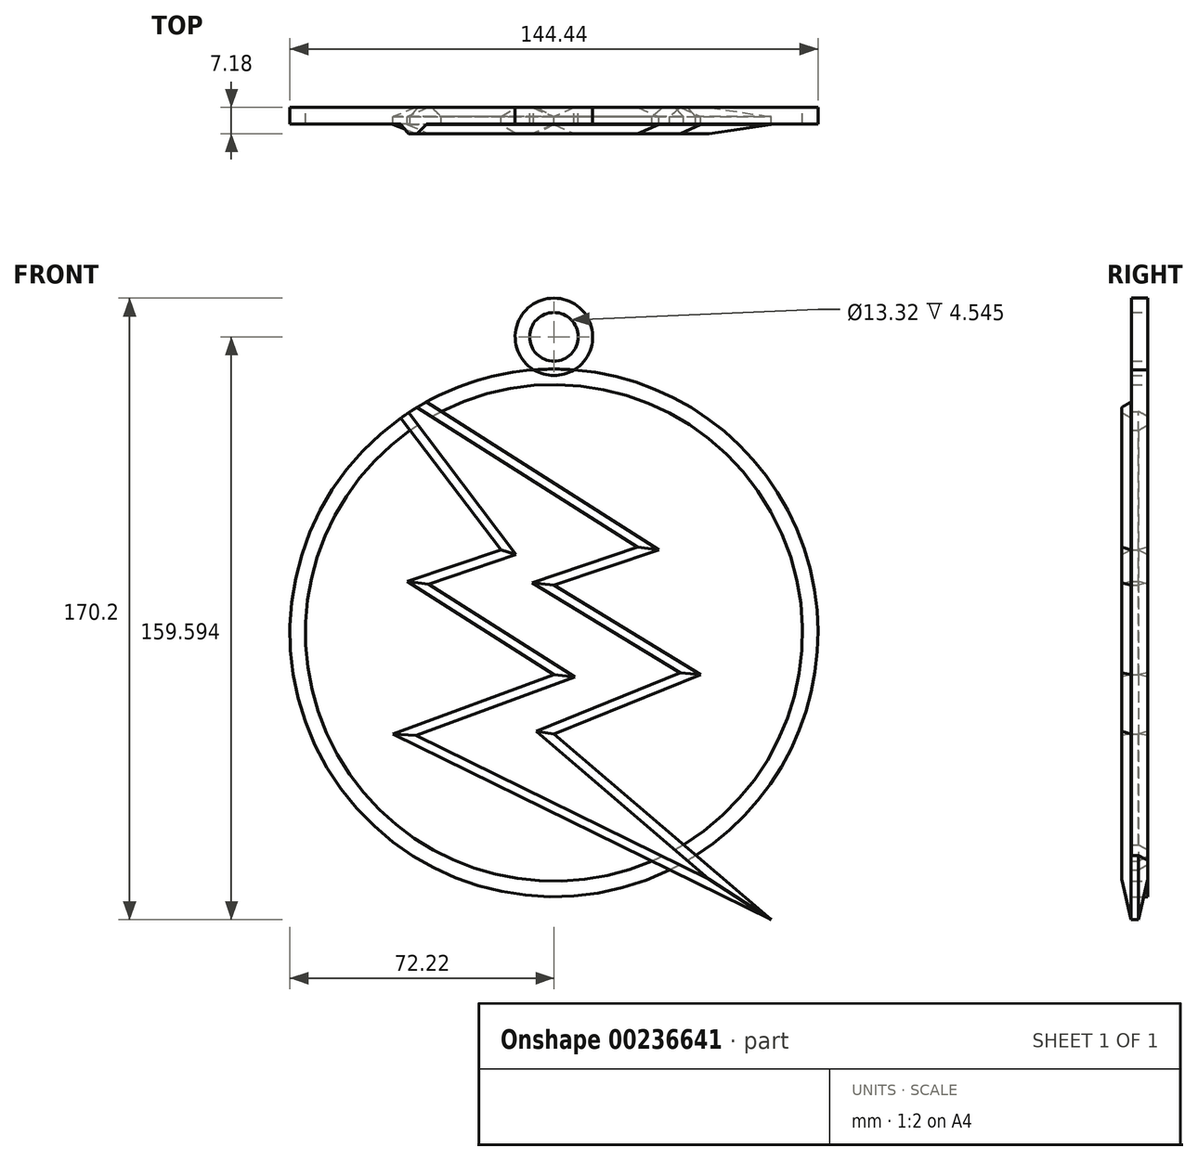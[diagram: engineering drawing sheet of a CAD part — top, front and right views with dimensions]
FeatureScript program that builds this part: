
annotation { "Feature Type Name" : "Feature", "Feature Type Description" : "" }
export const myFeature = defineFeature(function(context is Context, id is Id, definition is map)
    precondition{}
    {
        {
            var Q0;
            Q0=qCreatedBy(makeId("Front.planeOp"),FACE);
            var sketch = newSketch(context, id + "F0", { "sketchPlane" : qUnion([Q0])});
            skCircle(sketch, "E0", {"center": v(0, 0) * mm, "radius": 72.22 * mm});
            skCircle(sketch, "E1", {"center": v(0, 0) * mm, "radius": 67.99 * mm});
            skLineSegment(sketch, "E2", {"start": v(-54.7, 75.8) * mm, "end": v(28.75, 22.73) * mm});
            skLineSegment(sketch, "E3", {"start": v(28.75, 22.73) * mm, "end": v(0, 13.04) * mm});
            skLineSegment(sketch, "E4", {"start": v(0, 13.04) * mm, "end": v(40.2, -11.4) * mm});
            skLineSegment(sketch, "E5", {"start": v(40.2, -11.4) * mm, "end": v(0, -27.72) * mm});
            skLineSegment(sketch, "E6", {"start": v(0, -27.72) * mm, "end": v(59.4, -78.53) * mm});
            skLineSegment(sketch, "E7", {"start": v(59.4, -78.53) * mm, "end": v(-44.1, -27.72) * mm});
            skLineSegment(sketch, "E8", {"start": v(-44.1, -27.72) * mm, "end": v(0, -11.4) * mm});
            skLineSegment(sketch, "E9", {"start": v(0, -11.4) * mm, "end": v(-40.11, 14.1) * mm});
            skLineSegment(sketch, "E10", {"start": v(-40.11, 14.1) * mm, "end": v(-14.52, 22.73) * mm});
            skLineSegment(sketch, "E11", {"start": v(-14.52, 22.73) * mm, "end": v(-54.7, 75.8) * mm});
            skCircle(sketch, "E12", {"center": v(0, 81.06) * mm, "radius": 10.6 * mm});
            skCircle(sketch, "E13", {"center": v(0, 81.06) * mm, "radius": 6.66 * mm});
            skSolve(sketch);
        }
        {
            var Q0;
            {var subQ0=sQuery(id+"F0.wireOp",EDGE,"E11");var subQ1=sQuery(id+"F0.wireOp",EDGE,"E0");var subQ2=makeQuery(id+"F0.imprint","INTERSECT",VERTEX,{"derivedFrom":[subQ1,subQ0]});Q0=makeQuery(id+"F0.imprint","IMPRINT",FACE,{"disambiguationData":[TD([[makeQuery(id+"F0.imprint","IMPRINT",EDGE,{"disambiguationData":[TD([[subQ2,1.0]])],"derivedFrom":subQ1}),-1.0]])]});}
            var sketch = newSketch(context, id + "F1", { "sketchPlane" : qUnion([Q0])});
            skSolve(sketch);
        }
        {
            var Q0;
            {var subQ11=sQuery(id+"F0.wireOp",EDGE,"E3");Q0=makeQuery(id+"F0.imprint","IMPRINT",FACE,{"disambiguationData":[TD([[makeQuery(id+"F0.imprint","IMPRINT",EDGE,{"derivedFrom":subQ11}),-1.0]])]});}
            var Q1;
            {var subQ0=sQuery(id+"F0.wireOp",EDGE,"E7");var subQ1=sQuery(id+"F0.wireOp",EDGE,"E0");var subQ2=makeQuery(id+"F0.imprint","INTERSECT",VERTEX,{"derivedFrom":[subQ1,subQ0]});Q1=makeQuery(id+"F0.imprint","IMPRINT",FACE,{"disambiguationData":[TD([[makeQuery(id+"F0.imprint","IMPRINT",EDGE,{"disambiguationData":[TD([[subQ2,-1.0]])],"derivedFrom":subQ1}),1.0]])]});}
            var Q2;
            {var subQ0=sQuery(id+"F0.wireOp",EDGE,"E7");var subQ1=sQuery(id+"F0.wireOp",EDGE,"E0");var subQ2=makeQuery(id+"F0.imprint","INTERSECT",VERTEX,{"derivedFrom":[subQ1,subQ0]});Q2=makeQuery(id+"F0.imprint","IMPRINT",FACE,{"disambiguationData":[TD([[makeQuery(id+"F0.imprint","IMPRINT",EDGE,{"disambiguationData":[TD([[subQ2,-1.0]])],"derivedFrom":subQ1}),-1.0]])]});}
            var Q3;
            {var subQ0=sQuery(id+"F0.wireOp",EDGE,"E11");var subQ1=sQuery(id+"F0.wireOp",EDGE,"E0");var subQ2=makeQuery(id+"F0.imprint","INTERSECT",VERTEX,{"derivedFrom":[subQ1,subQ0]});Q3=makeQuery(id+"F1.imprint","IMPRINT",FACE,{"disambiguationData":[TD([[makeQuery(id+"F1.imprint","IMPRINT",EDGE,{"derivedFrom":makeQuery(id+"F0.imprint","IMPRINT",EDGE,{"disambiguationData":[TD([[subQ2,1.0]])],"derivedFrom":subQ1})}),-1.0]])]});}
            var Q4;
            {var subQ0=sQuery(id+"F0.wireOp",EDGE,"E11");var subQ1=sQuery(id+"F0.wireOp",EDGE,"E0");var subQ2=makeQuery(id+"F0.imprint","INTERSECT",VERTEX,{"derivedFrom":[subQ1,subQ0]});Q4=makeQuery(id+"F0.imprint","IMPRINT",FACE,{"disambiguationData":[TD([[makeQuery(id+"F0.imprint","IMPRINT",EDGE,{"disambiguationData":[TD([[subQ2,1.0]])],"derivedFrom":subQ1}),1.0]])]});}
            extrude(context, id + "F2", {"entities" : qUnion([Q0, Q1, Q2, Q3, Q4]), "depth" : 7.18 * mm});
        }
        {
            var Q0;
            {var subQ0=sQuery(id+"F0.wireOp",EDGE,"E2");var subQ1=sQuery(id+"F0.wireOp",EDGE,"E0");var subQ2=makeQuery(id+"F0.imprint","INTERSECT",VERTEX,{"derivedFrom":[subQ1,subQ0]});Q0=makeQuery(id+"F0.imprint","IMPRINT",FACE,{"disambiguationData":[TD([[makeQuery(id+"F0.imprint","IMPRINT",EDGE,{"disambiguationData":[TD([[subQ2,1.0]])],"derivedFrom":subQ1}),1.0]])]});}
            var Q1;
            {var subQ0=sQuery(id+"F0.wireOp",EDGE,"E11");var subQ1=sQuery(id+"F0.wireOp",EDGE,"E0");var subQ2=makeQuery(id+"F0.imprint","INTERSECT",VERTEX,{"derivedFrom":[subQ1,subQ0]});Q1=makeQuery(id+"F0.imprint","IMPRINT",FACE,{"disambiguationData":[TD([[makeQuery(id+"F0.imprint","IMPRINT",EDGE,{"disambiguationData":[TD([[subQ2,-1.0]])],"derivedFrom":subQ1}),1.0]])]});}
            var Q2;
            Q2=makeQuery(id+"F0.imprint","IMPRINT",FACE,{"disambiguationData":[TD([[makeQuery(id+"F0.imprint","IMPRINT",EDGE,{"derivedFrom":sQuery(id+"F0.wireOp",EDGE,"E13")}),-1.0]])]});
            var Q3;
            {var subQ0=sQuery(id+"F0.wireOp",EDGE,"E12");var subQ1=sQuery(id+"F0.wireOp",EDGE,"E0");var subQ2=makeQuery(id+"F0.imprint","INTERSECT",VERTEX,{"disambiguationData":[OD(0.0)],"derivedFrom":[subQ1,subQ0]});Q3=makeQuery(id+"F0.imprint","IMPRINT",FACE,{"disambiguationData":[TD([[makeQuery(id+"F0.imprint","IMPRINT",EDGE,{"disambiguationData":[TD([[subQ2,1.0]])],"derivedFrom":subQ1}),1.0]])]});}
            extrude(context, id + "F3", {"entities" : qUnion([Q0, Q1, Q2, Q3]), "operationType" : NewBodyOperationType.ADD, "depth" : 4.55 * mm});
        }
        {
            var Q0;
            Q0=makeQuery(id+"F2.opExtrude","CAP_EDGE",EDGE,{"disambiguationData":[OSD([sQuery(id+"F0.wireOp",EDGE,"E7")])],"isStart":false});
            var Q1;
            Q1=makeQuery(id+"F2.opExtrude","CAP_EDGE",EDGE,{"disambiguationData":[OSD([sQuery(id+"F0.wireOp",EDGE,"E9")])],"isStart":false});
            var Q2;
            {var subQ0=sQuery(id+"F0.wireOp",EDGE,"E11");Q2=makeQuery(id+"F2.opExtrude","CAP_EDGE",EDGE,{"disambiguationData":[OSD([subQ0]),TDD([makeQuery(id+"F0.imprint","IMPRINT",EDGE,{"disambiguationData":[TD([[makeQuery(id+"F0.imprint","INTERSECT",VERTEX,{"derivedFrom":[sQuery(id+"F0.wireOp",EDGE,"E10"),subQ0]}),-1.0]])],"derivedFrom":subQ0}),makeQuery(id+"F0.imprint","IMPRINT",EDGE,{"disambiguationData":[TD([[makeQuery(id+"F0.imprint","INTERSECT",VERTEX,{"derivedFrom":[sQuery(id+"F0.wireOp",EDGE,"E0"),subQ0]}),1.0]])],"derivedFrom":subQ0})])],"isStart":false});}
            var Q3;
            {var subQ0=sQuery(id+"F0.wireOp",EDGE,"E11");Q3=makeQuery(id+"F2.opExtrude","CAP_EDGE",EDGE,{"disambiguationData":[OSD([subQ0]),TDD([makeQuery(id+"F1.imprint","IMPRINT",EDGE,{"derivedFrom":makeQuery(id+"F0.imprint","IMPRINT",EDGE,{"disambiguationData":[TD([[makeQuery(id+"F0.imprint","INTERSECT",VERTEX,{"derivedFrom":[sQuery(id+"F0.wireOp",EDGE,"E2"),subQ0]}),1.0]])],"derivedFrom":subQ0})})])],"isStart":false});}
            var Q4;
            Q4=makeQuery(id+"F2.opExtrude","CAP_EDGE",EDGE,{"disambiguationData":[OSD([sQuery(id+"F0.wireOp",EDGE,"E6")])],"isStart":false});
            var Q5;
            Q5=makeQuery(id+"F2.opExtrude","CAP_EDGE",EDGE,{"disambiguationData":[OSD([sQuery(id+"F0.wireOp",EDGE,"E4")])],"isStart":false});
            var Q6;
            {var subQ0=sQuery(id+"F0.wireOp",EDGE,"E2");Q6=makeQuery(id+"F2.opExtrude","CAP_EDGE",EDGE,{"disambiguationData":[OSD([subQ0]),TDD([makeQuery(id+"F0.imprint","IMPRINT",EDGE,{"disambiguationData":[TD([[makeQuery(id+"F0.imprint","INTERSECT",VERTEX,{"derivedFrom":[sQuery(id+"F0.wireOp",EDGE,"E0"),subQ0]}),-1.0]])],"derivedFrom":subQ0}),makeQuery(id+"F0.imprint","IMPRINT",EDGE,{"disambiguationData":[TD([[makeQuery(id+"F0.imprint","INTERSECT",VERTEX,{"derivedFrom":[subQ0,sQuery(id+"F0.wireOp",EDGE,"E3")]}),1.0]])],"derivedFrom":subQ0})])],"isStart":false});}
            var Q7;
            Q7=makeQuery(id+"F2.opExtrude","CAP_EDGE",EDGE,{"disambiguationData":[OSD([sQuery(id+"F0.wireOp",EDGE,"E5")])],"isStart":false});
            var Q8;
            Q8=makeQuery(id+"F2.opExtrude","CAP_EDGE",EDGE,{"disambiguationData":[OSD([sQuery(id+"F0.wireOp",EDGE,"E3")])],"isStart":false});
            var Q9;
            Q9=makeQuery(id+"F2.opExtrude","CAP_EDGE",EDGE,{"disambiguationData":[OSD([sQuery(id+"F0.wireOp",EDGE,"E8")])],"isStart":false});
            var Q10;
            {var subQ0=sQuery(id+"F0.wireOp",EDGE,"E2");Q10=makeQuery(id+"F2.opExtrude","CAP_EDGE",EDGE,{"disambiguationData":[OSD([subQ0]),TDD([makeQuery(id+"F1.imprint","IMPRINT",EDGE,{"derivedFrom":makeQuery(id+"F0.imprint","IMPRINT",EDGE,{"disambiguationData":[TD([[makeQuery(id+"F0.imprint","INTERSECT",VERTEX,{"derivedFrom":[subQ0,sQuery(id+"F0.wireOp",EDGE,"E11")]}),-1.0]])],"derivedFrom":subQ0})})])],"isStart":false});}
            var Q11;
            Q11=makeQuery(id+"F2.opExtrude","CAP_EDGE",EDGE,{"disambiguationData":[OSD([sQuery(id+"F0.wireOp",EDGE,"E10")])],"isStart":false});
            var Q12;
            {var subQ0=sQuery(id+"F0.wireOp",EDGE,"E2");Q12=makeQuery(id+"F2.opExtrude","CAP_EDGE",EDGE,{"disambiguationData":[OSD([subQ0]),TDD([makeQuery(id+"F0.imprint","IMPRINT",EDGE,{"disambiguationData":[TD([[makeQuery(id+"F0.imprint","INTERSECT",VERTEX,{"derivedFrom":[sQuery(id+"F0.wireOp",EDGE,"E0"),subQ0]}),-1.0]])],"derivedFrom":subQ0}),makeQuery(id+"F0.imprint","IMPRINT",EDGE,{"disambiguationData":[TD([[makeQuery(id+"F0.imprint","INTERSECT",VERTEX,{"derivedFrom":[subQ0,sQuery(id+"F0.wireOp",EDGE,"E3")]}),1.0]])],"derivedFrom":subQ0})])],"isStart":true});}
            var Q13;
            {var subQ0=sQuery(id+"F0.wireOp",EDGE,"E2");Q13=makeQuery(id+"F2.opExtrude","CAP_EDGE",EDGE,{"disambiguationData":[OSD([subQ0]),TDD([makeQuery(id+"F1.imprint","IMPRINT",EDGE,{"derivedFrom":makeQuery(id+"F0.imprint","IMPRINT",EDGE,{"disambiguationData":[TD([[makeQuery(id+"F0.imprint","INTERSECT",VERTEX,{"derivedFrom":[subQ0,sQuery(id+"F0.wireOp",EDGE,"E11")]}),-1.0]])],"derivedFrom":subQ0})})])],"isStart":true});}
            var Q14;
            {var subQ0=sQuery(id+"F0.wireOp",EDGE,"E11");Q14=makeQuery(id+"F2.opExtrude","CAP_EDGE",EDGE,{"disambiguationData":[OSD([subQ0]),TDD([makeQuery(id+"F1.imprint","IMPRINT",EDGE,{"derivedFrom":makeQuery(id+"F0.imprint","IMPRINT",EDGE,{"disambiguationData":[TD([[makeQuery(id+"F0.imprint","INTERSECT",VERTEX,{"derivedFrom":[sQuery(id+"F0.wireOp",EDGE,"E2"),subQ0]}),1.0]])],"derivedFrom":subQ0})})])],"isStart":true});}
            var Q15;
            {var subQ0=sQuery(id+"F0.wireOp",EDGE,"E11");Q15=makeQuery(id+"F2.opExtrude","CAP_EDGE",EDGE,{"disambiguationData":[OSD([subQ0]),TDD([makeQuery(id+"F0.imprint","IMPRINT",EDGE,{"disambiguationData":[TD([[makeQuery(id+"F0.imprint","INTERSECT",VERTEX,{"derivedFrom":[sQuery(id+"F0.wireOp",EDGE,"E10"),subQ0]}),-1.0]])],"derivedFrom":subQ0}),makeQuery(id+"F0.imprint","IMPRINT",EDGE,{"disambiguationData":[TD([[makeQuery(id+"F0.imprint","INTERSECT",VERTEX,{"derivedFrom":[sQuery(id+"F0.wireOp",EDGE,"E0"),subQ0]}),1.0]])],"derivedFrom":subQ0})])],"isStart":true});}
            var Q16;
            Q16=makeQuery(id+"F2.opExtrude","CAP_EDGE",EDGE,{"disambiguationData":[OSD([sQuery(id+"F0.wireOp",EDGE,"E9")])],"isStart":true});
            var Q17;
            {var subQ0=sQuery(id+"F0.wireOp",EDGE,"E7");var subQ5=sQuery(id+"F0.wireOp",EDGE,"E8");Q17=makeQuery(id+"F3.boolean.opBoolean","SPLIT",EDGE,{"disambiguationData":[TD([makeQuery(id+"F2.opExtrude","SWEPT_FACE",FACE,{"disambiguationData":[OSD([subQ5])]})])],"derivedFrom":makeQuery(id+"F2.opExtrude","CAP_EDGE",EDGE,{"disambiguationData":[OSD([subQ0])],"isStart":true})});}
            var Q18;
            {var subQ0=sQuery(id+"F0.wireOp",EDGE,"E6");var subQ2=sQuery(id+"F0.wireOp",EDGE,"E7");Q18=makeQuery(id+"F3.boolean.opBoolean","SPLIT",EDGE,{"disambiguationData":[TD([makeQuery(id+"F2.opExtrude","SWEPT_FACE",FACE,{"disambiguationData":[OSD([subQ0])]})])],"derivedFrom":makeQuery(id+"F2.opExtrude","CAP_EDGE",EDGE,{"disambiguationData":[OSD([subQ2])],"isStart":true})});}
            var Q19;
            {var subQ0=sQuery(id+"F0.wireOp",EDGE,"E7");var subQ3=sQuery(id+"F0.wireOp",EDGE,"E6");Q19=makeQuery(id+"F3.boolean.opBoolean","SPLIT",EDGE,{"disambiguationData":[TD([makeQuery(id+"F2.opExtrude","SWEPT_FACE",FACE,{"disambiguationData":[OSD([subQ0])]})])],"derivedFrom":makeQuery(id+"F2.opExtrude","CAP_EDGE",EDGE,{"disambiguationData":[OSD([subQ3])],"isStart":true})});}
            var Q20;
            {var subQ0=sQuery(id+"F0.wireOp",EDGE,"E6");var subQ1=sQuery(id+"F0.wireOp",EDGE,"E5");Q20=makeQuery(id+"F3.boolean.opBoolean","SPLIT",EDGE,{"disambiguationData":[TD([makeQuery(id+"F2.opExtrude","SWEPT_FACE",FACE,{"disambiguationData":[OSD([subQ1])]})])],"derivedFrom":makeQuery(id+"F2.opExtrude","CAP_EDGE",EDGE,{"disambiguationData":[OSD([subQ0])],"isStart":true})});}
            var Q21;
            Q21=makeQuery(id+"F2.opExtrude","CAP_EDGE",EDGE,{"disambiguationData":[OSD([sQuery(id+"F0.wireOp",EDGE,"E5")])],"isStart":true});
            var Q22;
            Q22=makeQuery(id+"F2.opExtrude","CAP_EDGE",EDGE,{"disambiguationData":[OSD([sQuery(id+"F0.wireOp",EDGE,"E4")])],"isStart":true});
            var Q23;
            Q23=makeQuery(id+"F2.opExtrude","CAP_EDGE",EDGE,{"disambiguationData":[OSD([sQuery(id+"F0.wireOp",EDGE,"E3")])],"isStart":true});
            var Q24;
            Q24=makeQuery(id+"F2.opExtrude","CAP_EDGE",EDGE,{"disambiguationData":[OSD([sQuery(id+"F0.wireOp",EDGE,"E10")])],"isStart":true});
            var Q25;
            Q25=makeQuery(id+"F2.opExtrude","CAP_EDGE",EDGE,{"disambiguationData":[OSD([sQuery(id+"F0.wireOp",EDGE,"E8")])],"isStart":true});
            chamfer(context, id + "F4", {"entities" : qUnion([Q0, Q1, Q2, Q3, Q4, Q5, Q6, Q7, Q8, Q9, Q10, Q11, Q12, Q13, Q14, Q15, Q16, Q17, Q18, Q19, Q20, Q21, Q22, Q23, Q24, Q25]), "width" : 2.54 * mm, "tangentPropagation" : true});
        }
    });
